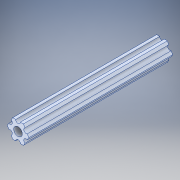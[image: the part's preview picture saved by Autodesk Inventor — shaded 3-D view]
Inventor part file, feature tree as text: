
AUTODESK INVENTOR PART (.ipt)
format: ipt  version: 2017 (Build 210142000, 142)  size: 161,280 bytes
history: native  units: in
note: dims shown in document units (in); Inventor stores cm internally (conversion verified against a paired STEP export)
features: other x1, extrude x1, sketch x1, projected_geometry x1
ambient origin geometry x8: Origin, YZ Plane, XZ Plane, XY Plane, X Axis, Y Axis, Z Axis, Center Point
bodies: Solid1 (feature_tree)
feature tree (4):
  other  "Boss-Extrude1"
  extrude  "Extrusion1"  [1 undecoded]
  sketch  "Sketch1"  dims[d0=3.875in d1=0.0in]
  projected_geometry  "Projected Loop1"
note: 1 required parameter value undecoded (feature->parameter linkage not recoverable at this tier; creation-order binding heuristic only, values carry confidence <= 0.55)
